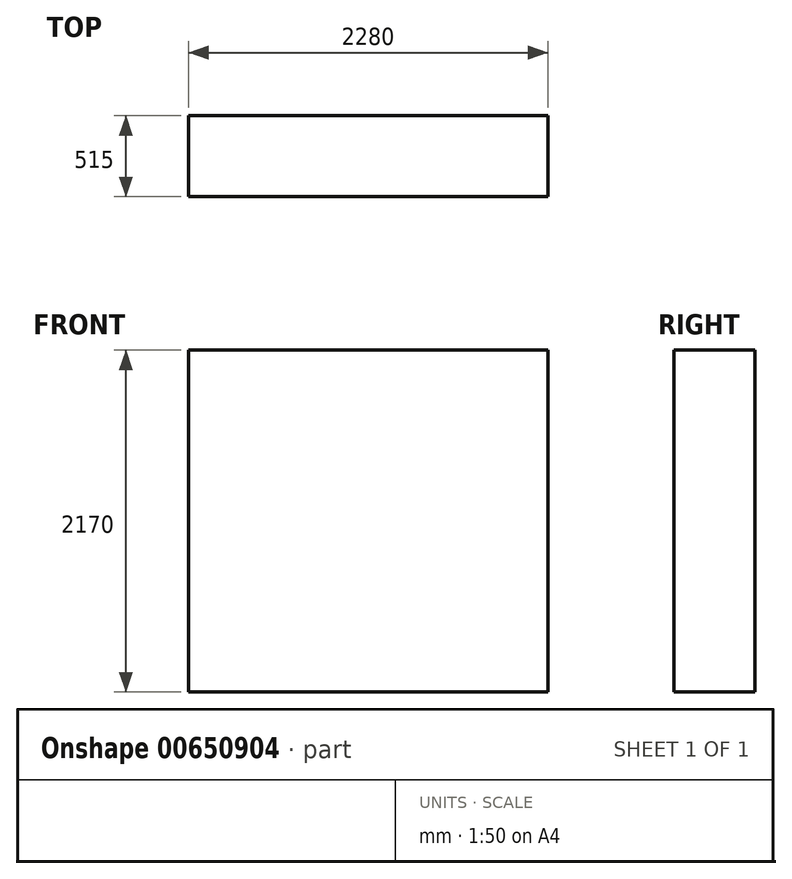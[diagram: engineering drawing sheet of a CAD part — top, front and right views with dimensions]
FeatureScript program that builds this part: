
annotation { "Feature Type Name" : "Feature", "Feature Type Description" : "" }
export const myFeature = defineFeature(function(context is Context, id is Id, definition is map)
    precondition{}
    {
        {
            var Q0;
            Q0=qCreatedBy(makeId("Top.planeOp"),FACE);
            var sketch = newSketch(context, id + "F0", { "sketchPlane" : qUnion([Q0])});
            skLineSegment(sketch, "E0.bottom", {"start": v(-334.59, 258.98) * mm, "end": v(1945.41, 258.98) * mm});
            skLineSegment(sketch, "E0.top", {"start": v(-334.59, -256.02) * mm, "end": v(1945.41, -256.02) * mm});
            skLineSegment(sketch, "E0.left", {"start": v(-334.59, 258.98) * mm, "end": v(-334.59, -256.02) * mm});
            skLineSegment(sketch, "E0.right", {"start": v(1945.41, 258.98) * mm, "end": v(1945.41, -256.02) * mm});
            skSolve(sketch);
        }
        {
            var Q0;
            Q0=makeQuery(id+"F0.imprint","IMPRINT",FACE,{"disambiguationData":[TD([[makeQuery(id+"F0.imprint","IMPRINT",EDGE,{"derivedFrom":sQuery(id+"F0.wireOp",EDGE,"E0.bottom")}),-1.0]])]});
            extrude(context, id + "F1", {"entities" : qUnion([Q0]), "depth" : 2170 * mm, "offsetDistance" : 25 * mm});
        }
    });
